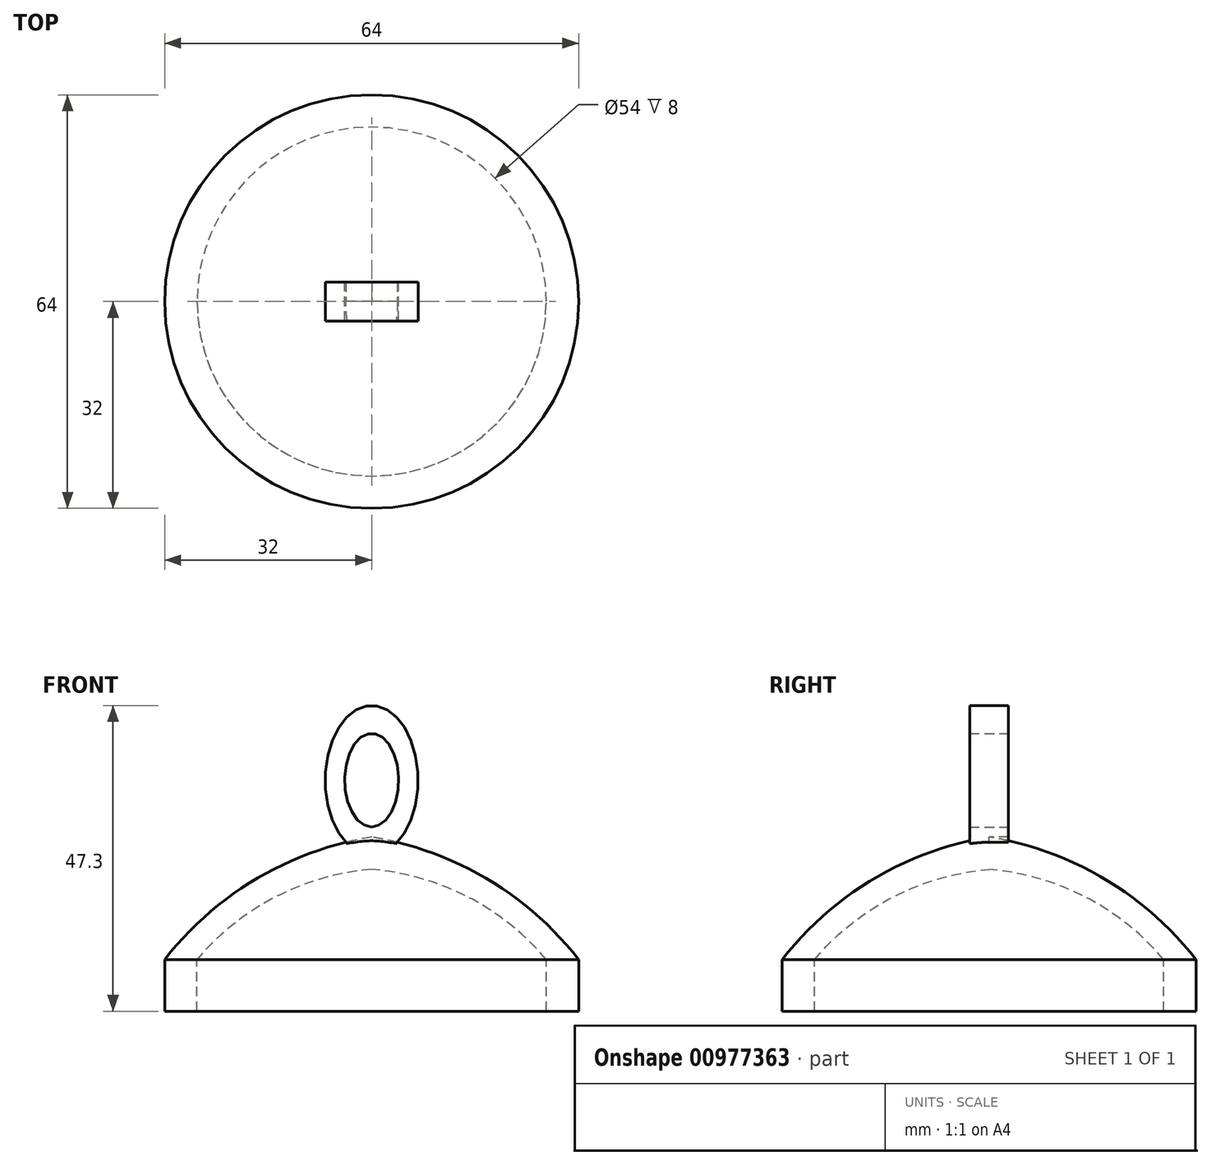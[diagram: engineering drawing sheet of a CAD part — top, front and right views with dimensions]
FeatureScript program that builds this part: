
annotation { "Feature Type Name" : "Feature", "Feature Type Description" : "" }
export const myFeature = defineFeature(function(context is Context, id is Id, definition is map)
    precondition{}
    {
        {
            var Q0;
            Q0=qCreatedBy(makeId("Front.planeOp"),FACE);
            var sketch = newSketch(context, id + "F0", { "sketchPlane" : qUnion([Q0])});
            skArc(sketch, "E0", {"start": v(0, 18.95) * mm, "mid": v(-17.79, 12.5) * mm, "end": v(-32, 0) * mm});
            skLineSegment(sketch, "E1", {"start": v(0, 18.95) * mm, "end": v(0, 13.95) * mm});
            skLineSegment(sketch, "E2", {"start": v(-32, 0) * mm, "end": v(-27, 0) * mm});
            skArc(sketch, "E3", {"start": v(0, 13.95) * mm, "mid": v(-14.89, 9.66) * mm, "end": v(-27, 0) * mm});
            skSolve(sketch);
        }
        {
            var Q0;
            Q0 = qSketchRegion(id + "F0", true);
            var Q1;
            Q1=sQuery(id+"F0.wireOp",EDGE,"E1");
            revolve(context, id + "F1", {"surfaceOperationType" : NewSurfaceOperationType.NEW, "entities" : qUnion([Q0]), "axis" : qUnion([Q1]), "revolveType" : RevolveType.FULL});
        }
        {
            var Q0;
            Q0=makeQuery(id+"F1.opRevolve","SWEPT_FACE",FACE,{"disambiguationData":[OSD([sQuery(id+"F0.wireOp",EDGE,"E2")])]});
            extrude(context, id + "F2", {"entities" : qUnion([Q0]), "operationType" : NewBodyOperationType.ADD, "depth" : 8 * mm, "offsetDistance" : 25 * mm});
        }
        {
            var Q0;
            Q0=qCreatedBy(makeId("Front.planeOp"),FACE);
            var sketch = newSketch(context, id + "F3", { "sketchPlane" : qUnion([Q0])});
            skEllipse(sketch, "E4", {"center": v(0, 27.74) * mm, "majorRadius": 11.56 * mm, "minorRadius": 7.17 * mm, "majorAxis": v(0, -1)});
            skEllipse(sketch, "E5", {"center": v(0, 27.74) * mm, "majorRadius": 7.22 * mm, "minorRadius": 4.18 * mm, "majorAxis": v(0, -1)});
            skSolve(sketch);
        }
        {
            var Q0;
            Q0 = qSketchRegion(id + "F3", true);
            extrude(context, id + "F4", {"entities" : qUnion([Q0]), "operationType" : NewBodyOperationType.ADD, "depth" : 3 * mm, "offsetDistance" : 25 * mm});
        }
        {
            var Q0;
            Q0=makeQuery(id+"F4.opExtrude","CAP_FACE",FACE,{"disambiguationData":[OSD([sQuery(id+"F3.wireOp",EDGE,"E4"),sQuery(id+"F3.wireOp",EDGE,"E5")])],"isStart":true});
            extrude(context, id + "F5", {"entities" : qUnion([Q0]), "operationType" : NewBodyOperationType.ADD, "depth" : 3 * mm, "offsetDistance" : 25 * mm});
        }
    });
